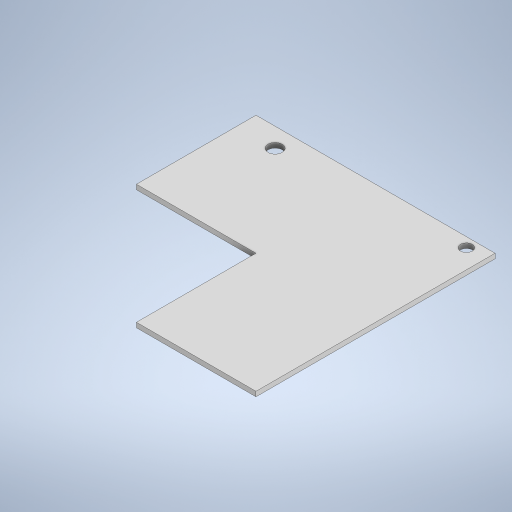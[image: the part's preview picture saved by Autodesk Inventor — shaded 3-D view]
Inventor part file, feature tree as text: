
AUTODESK INVENTOR PART (.ipt)
format: ipt  version: 2023 (Build 270158000, 158)  size: 235,520 bytes
history: native  units: mm
features: extrude x1, sketch x1
ambient origin geometry x8: Origin, YZ Plane, XZ Plane, XY Plane, X Axis, Y Axis, Z Axis, Center Point
bodies: Solid1 (feature_tree)
feature tree (2):
  extrude  "Extrusion1"  Depth=50.0mm
  sketch  "Sketch1"  dims[d0=100.0mm d1=50.0mm d2=50.0mm d3=50.0mm d4=10.0mm d5=10.0mm d6=10.0mm d7=10.0mm d8=6.0mm d9=5.0mm d10=2.0mm d11=0.0mm]
